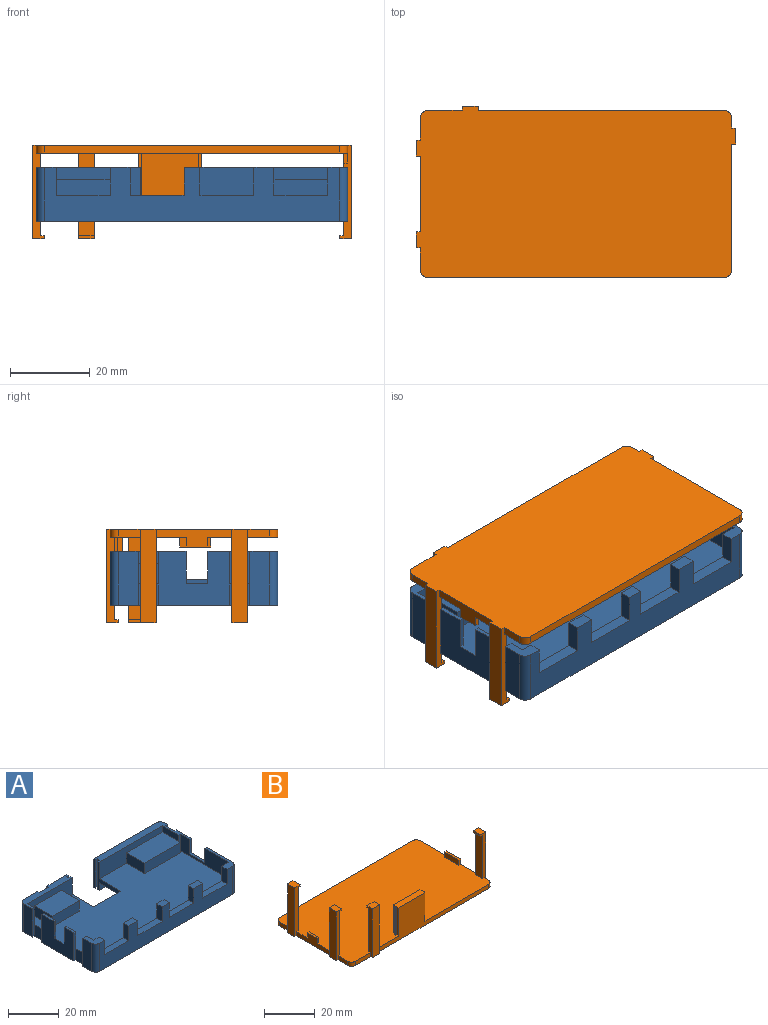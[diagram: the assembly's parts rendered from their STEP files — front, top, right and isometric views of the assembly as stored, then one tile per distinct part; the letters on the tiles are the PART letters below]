
ASSEMBLY  parts=2 mates=1
PART A: 107 faces, bbox 78x42x13.5 mm
  f0: plane 35x8mm, normal (0,-1,0), area 180mm2, adj f1,f2,f20,f53,f75,f77
  f1: plane 9x3mm, normal (-1,0,0), area 27mm2, adj f0,f52,f53,f77
  f2: plane 77x36mm, normal (0,0,1), area 2198.5mm2, adj f0,f3,f4,f20,f21,f22,f34,f36
  f3: plane 25x8mm, normal (0,-1,0), area 125mm2, adj f2,f22,f42,f43,f70,f71,f73
  f4: plane 27x8mm, normal (-1,0,0), area 156.5mm2, adj f2,f6,f7,f8,f52,f53,f54,f58
  f5: plane 31x13.5mm, normal (1,0,0), area 359mm2, adj f6,f7,f8,f11,f53,f54,f101,f102
  f6: plane 8.5x1mm, normal (0,0,1), area 8.5mm2, adj f4,f5,f7,f8
  f7: plane 7x1mm, normal (0,1,0), area 7mm2, adj f4,f5,f6,f54
  f8: plane 7x1mm, normal (0,-1,0), area 7mm2, adj f4,f5,f6,f53
  f9: plane 7x3mm, normal (1,0,0), area 21mm2, adj f51,f56,f58,f59
  f10: plane 7x3mm, normal (-1,0,0), area 21mm2, adj f54,f58,f59,f60
  f11: plane 13.5x1mm, normal (0,1,0), area 13.5mm2, adj f5,f12,f53,f101
  f12: plane 13.5x5mm, normal (1,0,0), area 67.5mm2, adj f11,f13,f53,f101
  f13: plane 13.5x1mm, normal (0,-1,0), area 13.5mm2, adj f12,f14,f53,f101
  f14: plane 13.5x2mm, normal (1,0,0), area 27mm2, adj f13,f53,f101,f103
  f15: plane 35x13.5mm, normal (0,1,0), area 472.5mm2, adj f16,f53,f101,f103
  f16: plane 13.5x0.9mm, normal (-1,0,0), area 12.2mm2, adj f15,f17,f53,f101
  f17: plane 13.5x1mm, normal (0,-1,0), area 13.5mm2, adj f16,f18,f53,f101
  f18: plane 13.5x1.2mm, normal (-1,0,0), area 16.2mm2, adj f17,f19,f53,f101
  f19: plane 13.5x1mm, normal (0,1,0), area 13.5mm2, adj f18,f20,f53,f101
  f20: plane 13.5x12.9mm, normal (-1,0,0), area 36.1mm2, adj f0,f2,f19,f21,f41,f53,f100,f101
  f21: plane 15x2mm, normal (0,1,0), area 30mm2, adj f2,f20,f22,f41
  f22: plane 13.5x12.9mm, normal (1,0,0), area 36.1mm2, adj f2,f3,f21,f23,f41,f43,f94,f101
  f23: plane 13.5x1mm, normal (0,1,0), area 13.5mm2, adj f22,f24,f43,f101
  f24: plane 13.5x1.2mm, normal (1,0,0), area 16.2mm2, adj f23,f25,f43,f101
  f25: plane 13.5x1mm, normal (0,-1,0), area 13.5mm2, adj f24,f26,f43,f101
  f26: plane 13.5x0.9mm, normal (1,0,0), area 12.2mm2, adj f25,f27,f43,f101
  f27: plane 13.5x11mm, normal (0,1,0), area 148.5mm2, adj f26,f28,f43,f101
  f28: plane 13.5x1mm, normal (-1,0,0), area 13.5mm2, adj f27,f29,f43,f101
  f29: plane 13.5x5mm, normal (0,1,0), area 67.5mm2, adj f28,f30,f43,f101
  f30: plane 13.5x1mm, normal (1,0,0), area 13.5mm2, adj f29,f31,f43,f101
  f31: plane 13.5x8mm, normal (0,1,0), area 108mm2, adj f30,f43,f101,f104
  f32: plane 13.5x5mm, normal (-1,0,0), area 67.5mm2, adj f33,f43,f101,f104
  f33: plane 13.5x1mm, normal (0,-1,0), area 13.5mm2, adj f32,f34,f42,f43,f101
  f34: plane 5.5x5mm, normal (-1,0,0), area 27.5mm2, adj f2,f33,f35,f101
  f35: plane 13.5x1mm, normal (0,1,0), area 13.5mm2, adj f34,f36,f45,f46,f101
  f36: plane 18x13.5mm, normal (-1,0,0), area 199mm2, adj f2,f35,f37,f44,f46,f48,f49,f101
  f37: plane 13.5x1mm, normal (0,-1,0), area 13.5mm2, adj f36,f38,f47,f49,f101
  f38: plane 5.5x5mm, normal (-1,0,0), area 27.5mm2, adj f2,f37,f39,f101
  f39: plane 13.5x2mm, normal (0,1,0), area 21.5mm2, adj f2,f38,f40,f50,f51,f101
  f40: plane 13.5x5mm, normal (-1,0,0), area 67.5mm2, adj f39,f51,f101,f105
  f41: plane 75x38mm, normal (0,0,-1), area 2508.8mm2, adj f20,f21,f22,f79,f83,f87,f91,f94
  f42: plane 8x4mm, normal (1,0,0), area 32mm2, adj f2,f3,f33,f43
  f43: plane 26x7mm, normal (0,0,1), area 74.9mm2, adj f3,f22,f23,f24,f25,f26,f27,f28
  f44: plane 8x1mm, normal (0,-1,0), area 8mm2, adj f2,f36,f45,f46
  f45: plane 8x7mm, normal (1,0,0), area 56mm2, adj f2,f35,f44,f46
  f46: plane 7x1mm, normal (0,0,1), area 7mm2, adj f35,f36,f44,f45
  f47: plane 8x5.5mm, normal (1,0,0), area 44mm2, adj f2,f37,f48,f49
  f48: plane 8x1mm, normal (0,1,0), area 8mm2, adj f2,f36,f47,f49
  f49: plane 5.5x1mm, normal (0,0,1), area 5.5mm2, adj f36,f37,f47,f48
  f50: plane 8x4mm, normal (1,0,0), area 32mm2, adj f2,f39,f51,f58
  f51: plane 7x5mm, normal (0,0,1), area 22.1mm2, adj f9,f39,f40,f50,f58,f59,f105
  f52: plane 8x1mm, normal (0,-1,0), area 8mm2, adj f1,f2,f4,f53,f74
  f53: plane 37x17mm, normal (0,0,1), area 126.9mm2, adj f0,f1,f4,f5,f8,f11,f12,f13
  f54: plane 16.5x5mm, normal (0,0,1), area 27.6mm2, adj f4,f5,f7,f10,f58,f59,f102
  f55: plane 13.5x3mm, normal (0,0,1), area 40.5mm2, adj f58,f59,f65,f69
  f56: plane 13.5x3mm, normal (0,0,1), area 40.5mm2, adj f9,f58,f59,f68
  f57: plane 13.5x3mm, normal (0,0,1), area 40.5mm2, adj f58,f59,f62,f66
  f58: plane 75x8mm, normal (0,1,0), area 222mm2, adj f2,f4,f9,f10,f50,f51,f54,f55
  f59: plane 74x13.5mm, normal (0,-1,0), area 621mm2, adj f9,f10,f51,f54,f55,f56,f57,f60
  f60: plane 13.5x3mm, normal (0,0,1), area 40.5mm2, adj f10,f58,f59,f63
  f61: plane 5x3mm, normal (0,0,1), area 15mm2, adj f58,f59,f62,f63
  f62: plane 7x3mm, normal (-1,0,0), area 21mm2, adj f57,f58,f59,f61
  f63: plane 7x3mm, normal (1,0,0), area 21mm2, adj f58,f59,f60,f61
  f64: plane 4x3mm, normal (0,0,1), area 12mm2, adj f58,f59,f65,f66
  f65: plane 7x3mm, normal (-1,0,0), area 21mm2, adj f55,f58,f59,f64
  f66: plane 7x3mm, normal (1,0,0), area 21mm2, adj f57,f58,f59,f64
  f67: plane 5x3mm, normal (0,0,1), area 15mm2, adj f58,f59,f68,f69
  f68: plane 7x3mm, normal (-1,0,0), area 21mm2, adj f56,f58,f59,f67
  f69: plane 7x3mm, normal (1,0,0), area 21mm2, adj f55,f58,f59,f67
  f70: plane 10x5mm, normal (1,0,0), area 50mm2, adj f2,f3,f72,f73
  f71: plane 10x5mm, normal (-1,0,0), area 50mm2, adj f2,f3,f72,f73
  f72: plane 15x5mm, normal (0,-1,0), area 75mm2, adj f2,f70,f71,f73
  f73: plane 15x10mm, normal (0,0,1), area 150mm2, adj f3,f70,f71,f72
  f74: plane 5x1mm, normal (1,0,0), area 5mm2, adj f2,f52,f76,f77
  f75: plane 10x5mm, normal (-1,0,0), area 50mm2, adj f0,f2,f76,f77
  f76: plane 20x5mm, normal (0,-1,0), area 100mm2, adj f2,f74,f75,f77
  f77: plane 20x10mm, normal (0,0,1), area 200mm2, adj f0,f1,f74,f75,f76
  f78: cylinder r=1.7mm len=3.4mm, axis (0,0,1), area 21.4mm2, adj f80,f81
  f79: cylinder r=3.5mm len=7mm, axis (0,0,1), area 44mm2, adj f41,f80
  f80: plane 7x7mm, normal (0,0,-1), area 29.4mm2, adj f78,f79
  f81: plane 3.4x3.4mm, normal (0,0,-1), area 9.1mm2, adj f78
  f82: cylinder r=1.7mm len=3.4mm, axis (0,0,1), area 21.4mm2, adj f84,f85
  f83: cylinder r=3.5mm len=7mm, axis (0,0,1), area 44mm2, adj f41,f84
  f84: plane 7x7mm, normal (0,0,-1), area 29.4mm2, adj f82,f83
  f85: plane 3.4x3.4mm, normal (0,0,-1), area 9.1mm2, adj f82
  f86: cylinder r=1.7mm len=3.4mm, axis (0,0,1), area 21.4mm2, adj f88,f89
  f87: cylinder r=3.5mm len=7mm, axis (0,0,1), area 44mm2, adj f41,f88
  f88: plane 7x7mm, normal (0,0,-1), area 29.4mm2, adj f86,f87
  f89: plane 3.4x3.4mm, normal (0,0,-1), area 9.1mm2, adj f86
  f90: cylinder r=1.7mm len=3.4mm, axis (0,0,1), area 21.4mm2, adj f92,f93
  f91: cylinder r=3.5mm len=7mm, axis (0,0,1), area 44mm2, adj f41,f92
  f92: plane 7x7mm, normal (0,0,-1), area 29.4mm2, adj f90,f91
  f93: plane 3.4x3.4mm, normal (0,0,-1), area 9.1mm2, adj f90
  f94: plane 24x3.5mm, normal (0,-1,0), area 84mm2, adj f22,f41,f95,f101
  f95: plane 38x3.5mm, normal (1,0,0), area 133mm2, adj f41,f94,f96,f101
  f96: plane 74x3.5mm, normal (0,1,0), area 259mm2, adj f41,f95,f101,f106
  f97: plane 30x3.5mm, normal (-1,0,0), area 105mm2, adj f41,f98,f101,f106
  f98: plane 3.5x1mm, normal (0,-1,0), area 3.5mm2, adj f41,f97,f99,f101
  f99: plane 7x3.5mm, normal (-1,0,0), area 24.5mm2, adj f41,f98,f100,f101
  f100: plane 35x3.5mm, normal (0,-1,0), area 122.5mm2, adj f20,f41,f99,f101
  f101: plane 78x42mm, normal (0,0,-1), area 362.4mm2, adj f5,f11,f12,f13,f14,f15,f16,f17
  f102: cylinder r=2mm len=13.5mm, axis (0,0,-1), area 42.4mm2, adj f5,f54,f59,f101
  f103: cylinder r=2mm len=13.5mm, axis (0,0,-1), area 42.4mm2, adj f14,f15,f53,f101
  f104: cylinder r=2mm len=13.5mm, axis (0,0,-1), area 42.4mm2, adj f31,f32,f43,f101
  f105: cylinder r=2mm len=13.5mm, axis (0,0,-1), area 42.4mm2, adj f40,f51,f59,f101
  f106: cylinder r=1mm len=3.5mm, axis (0,0,-1), area 5.5mm2, adj f41,f96,f97,f101
PART B: 62 faces, bbox 80x43x23.5 mm
  f0: plane 20.7x4mm, normal (-1,0,0), area 82.8mm2, adj f1,f21,f22,f56
  f1: plane 78x42mm, normal (0,0,1), area 3198.8mm2, adj f0,f2,f3,f4,f5,f6,f7,f8
  f2: plane 5.5x2mm, normal (-1,0,0), area 11mm2, adj f1,f10,f25,f51
  f3: plane 2.5x2mm, normal (1,0,0), area 5mm2, adj f1,f10,f21,f52
  f4: plane 8.5x2mm, normal (0,-1,0), area 17mm2, adj f1,f10,f16,f51
  f5: plane 19x4.5mm, normal (-1,0,0), area 51.2mm2, adj f1,f10,f12,f27,f42,f44,f45
  f6: plane 74x2mm, normal (0,1,0), area 148mm2, adj f1,f10,f50,f53
  f7: plane 5.5x2mm, normal (-1,0,0), area 11mm2, adj f1,f10,f14,f50
  f8: plane 61.5x15.5mm, normal (0,-1,0), area 318.8mm2, adj f1,f10,f18,f30,f31,f41,f52
  f9: plane 31.5x4.5mm, normal (1,0,0), area 82.5mm2, adj f1,f10,f22,f46,f47,f49,f53
  f10: plane 80x43mm, normal (0,0,-1), area 3288.6mm2, adj f2,f3,f4,f5,f6,f7,f8,f9
  f11: plane 20.7x4mm, normal (1,0,0), area 82.8mm2, adj f1,f12,f14,f58
  f12: plane 23.5x3mm, normal (0,-1,0), area 45.8mm2, adj f1,f5,f10,f11,f13,f15,f58,f59
  f13: plane 23.5x4mm, normal (-1,0,0), area 94mm2, adj f10,f12,f14,f15
  f14: plane 23.5x3mm, normal (0,1,0), area 45.8mm2, adj f1,f7,f10,f11,f13,f15,f58,f59
  f15: plane 4x3mm, normal (0,0,1), area 12mm2, adj f12,f13,f14,f59
  f16: plane 23.5x3mm, normal (-1,0,0), area 45.8mm2, adj f1,f4,f10,f17,f19,f20,f54,f55
  f17: plane 20.7x4mm, normal (0,1,0), area 82.8mm2, adj f1,f16,f18,f54
  f18: plane 23.5x3mm, normal (1,0,0), area 45.8mm2, adj f1,f8,f10,f17,f19,f20,f54,f55
  f19: plane 23.5x4mm, normal (0,-1,0), area 94mm2, adj f10,f16,f18,f20
  f20: plane 4x3mm, normal (0,0,1), area 12mm2, adj f16,f18,f19,f55
  f21: plane 23.5x3mm, normal (0,-1,0), area 45.8mm2, adj f0,f1,f3,f10,f23,f24,f56,f57
  f22: plane 23.5x3mm, normal (0,1,0), area 45.8mm2, adj f0,f1,f9,f10,f23,f24,f56,f57
  f23: plane 23.5x4mm, normal (1,0,0), area 94mm2, adj f10,f21,f22,f24
  f24: plane 4x3mm, normal (0,0,1), area 12mm2, adj f21,f22,f23,f57
  f25: plane 23.5x3mm, normal (0,-1,0), area 45.8mm2, adj f1,f2,f10,f26,f28,f29,f60,f61
  f26: plane 23.5x4mm, normal (-1,0,0), area 94mm2, adj f10,f25,f27,f29
  f27: plane 23.5x3mm, normal (0,1,0), area 45.8mm2, adj f1,f5,f10,f26,f28,f29,f60,f61
  f28: plane 20.7x4mm, normal (1,0,0), area 82.8mm2, adj f1,f25,f27,f60
  f29: plane 4x3mm, normal (0,0,1), area 12mm2, adj f25,f26,f27,f61
  f30: plane 13.5x1.1mm, normal (-1,0,0), area 14.8mm2, adj f1,f8,f40,f41
  f31: plane 13.5x1.1mm, normal (1,0,0), area 14.8mm2, adj f1,f8,f32,f41
  f32: plane 13.5x0.7mm, normal (0,-1,0), area 9.4mm2, adj f1,f31,f33,f41
  f33: plane 13.5x0.8mm, normal (1,0,0), area 10.8mm2, adj f1,f32,f34,f41
  f34: plane 13.5x0.7mm, normal (0,1,0), area 9.4mm2, adj f1,f33,f35,f41
  f35: plane 13.5x1.1mm, normal (1,0,0), area 14.8mm2, adj f1,f34,f36,f41
  f36: plane 14.5x13.5mm, normal (0,1,0), area 195.8mm2, adj f1,f35,f37,f41
  f37: plane 13.5x1.1mm, normal (-1,0,0), area 14.8mm2, adj f1,f36,f38,f41
  f38: plane 13.5x0.7mm, normal (0,1,0), area 9.4mm2, adj f1,f37,f39,f41
  f39: plane 13.5x0.8mm, normal (-1,0,0), area 10.8mm2, adj f1,f38,f40,f41
  f40: plane 13.5x0.7mm, normal (0,-1,0), area 9.4mm2, adj f1,f30,f39,f41
  f41: plane 15.9x3mm, normal (0,0,1), area 44.6mm2, adj f8,f30,f31,f32,f33,f34,f35,f36
  f42: plane 2.5x1mm, normal (0,-1,0), area 2.5mm2, adj f1,f5,f43,f45
  f43: plane 5.3x2.5mm, normal (1,0,0), area 13.3mm2, adj f1,f42,f44,f45
  f44: plane 2.5x1mm, normal (0,1,0), area 2.5mm2, adj f1,f5,f43,f45
  f45: plane 5.3x1mm, normal (0,0,1), area 5.3mm2, adj f5,f42,f43,f44
  f46: plane 2.5x1mm, normal (0,-1,0), area 2.5mm2, adj f1,f9,f48,f49
  f47: plane 2.5x1mm, normal (0,1,0), area 2.5mm2, adj f1,f9,f48,f49
  f48: plane 7.8x2.5mm, normal (-1,0,0), area 19.5mm2, adj f1,f46,f47,f49
  f49: plane 7.8x1mm, normal (0,0,1), area 7.8mm2, adj f9,f46,f47,f48
  f50: cylinder r=2mm len=2mm, axis (0,0,-1), area 6.3mm2, adj f1,f6,f7,f10
  f51: cylinder r=2mm len=2mm, axis (0,0,1), area 6.3mm2, adj f1,f2,f4,f10
  f52: cylinder r=2mm len=2mm, axis (0,0,-1), area 6.3mm2, adj f1,f3,f8,f10
  f53: cylinder r=2mm len=2mm, axis (0,0,1), area 6.3mm2, adj f1,f6,f9,f10
  f54: plane 4x1mm, normal (0,0,-1), area 4mm2, adj f16,f17,f18,f55
  f55: plane 4x0.8mm, normal (0,1,0), area 3.2mm2, adj f16,f18,f20,f54
  f56: plane 4x1mm, normal (0,0,-1), area 4mm2, adj f0,f21,f22,f57
  f57: plane 4x0.8mm, normal (-1,0,0), area 3.2mm2, adj f21,f22,f24,f56
  f58: plane 4x1mm, normal (0,0,-1), area 4mm2, adj f11,f12,f14,f59
  f59: plane 4x0.8mm, normal (1,0,0), area 3.2mm2, adj f12,f14,f15,f58
  f60: plane 4x1mm, normal (0,0,-1), area 4mm2, adj f25,f27,f28,f61
  f61: plane 4x0.8mm, normal (1,0,0), area 3.2mm2, adj f25,f27,f29,f60
PLACE A t=(6.9,18.62,16.54)mm
PLACE B rot(axis=(1,0,0),180deg) t=(6.9,60.62,32.14)mm
MATE fastened B.f17 <-> A.f29  axis (0,-1,0) through (19.4,59.62,19.79)mm
